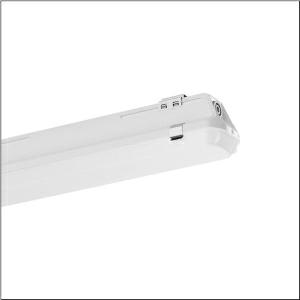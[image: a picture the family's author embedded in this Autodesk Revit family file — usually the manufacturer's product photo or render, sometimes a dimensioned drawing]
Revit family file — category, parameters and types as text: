
# Revit family: monsun_r__21_51fb10dp660b_51d9
name_source: partatom
category: Lighting Fixtures
units: mm (PartAtom-declared; Revit-internal decimal feet)

## family parameters
Cut with Voids When Loaded = No
Host = Face
Light Source = No
Part Type = Normal
Room Calculation Point = No
Round Connector Dimension = Use Diameter
Shared = No

## types (1)
- --- (1 x LED, 6060 lm, 39.4 W, 6500K)
    Apparent Load = 39 VA
    CIE Flux Codes = 47 77 93 94 100
    Color Rendering = 80
    Color Temperature = 6500K
    Default Elevation = 1800 mm
    Description = Monsun® 21, damp-proof luminaire, chain hanger, primary optical cover: enclosure, of PMMA, light emission: direct distribution, primary light characteristic: symmetric, installation type: suspended mounting, surface-mounted, horizontal mounting, vertical mounting, LED, rated luminous flux: 6.060lm, luminous efficacy: 154lm/W, light colour: 865, colour temperature: 6500K, control gear: ECG DALI, with terminal, 5-pole, max. 2.5mm², mains connection: 220..240V, AC, 50/60Hz, rated input power: 39W, housing, of glass-fibre reinforced polyester, uncoated, bright grey, incl. chain hanger, length: 1.590mm, width: 90mm, height: 88mm, clip for enclosure, of stainless steel (V2A), ceiling mounting element, of stainless steel (V2A), chain hanger, of stainless steel (V2A), protection rating (complete): IP66, insulation class (complete): insulation class I (protective earthing), certification: CE, ENEC, VDE, UKCA, protection symbol: D, impact resistance: IK04, permissible operating ambient temperature: -25..+35°C, standard: EN 50419, EN 60598-2-1, corresponds to IFS (International Featured Standards) requirements for safety and quality in the food industry, for indoor or canopied outdoor use, no direct snow, no direct sun, no direct rain, contact your sales advisor before using the luminaires in applications with unclear chemical exposure, large temperature fluctuations or condensation-forming humidity, LABS conformity tested according to VDMA 24364:2018-05, packaging unit: 1 piece
    Height = 89 mm
    Lamp = 1 x LED
    Lamp Light Flux = 6060 lm
    Lamp Power = 39.4 W
    Lamp count = 1
    Length = 1590 mm
    Luminous efficacy = 154 lm/W
    Manufacturer = Siteco
    ModVariant = No
    Model = 51FB10DP660B
    Mounting Place = Ceiling
    Mounting Type = Surface mounted
    Number of Poles = 1
    OnlyDefault = Yes
    Power Factor = 1
    Product Name = Monsun® 21
    Product group = damp-proof luminaire
    ProductGroupID = 301
    Protection Class = Protection class I
    Protection Degree = IP 66
    RLX_Detail_Level = 1
    RLX_Emergency_Light_Flux = 0 lm
    RLX_Emergency_Type = 0
    RLX_Emergency_Type_DB = No
    RlxData = <blob elided: 92413 chars, md5=59abc3b0>
    Socket = socket
    Standby Power = 0 W
    System Light Flux = 6060 lm
    System Power = 39 W
    Type Comments = factory setting: luminous flux: 100 % | dim-lin: 254 | 261 mA
    Type Image = l_1006717.jpg
    URL = http://relux.com
    VarID = @adj_152235
    Voltage = 0 V
    Weight = 0.00 kg
    Width = 90 mm

## geometry (parser evidence)
native form markers: Blend x4, Sweep x14
no freeform markers — native parametric forms only
